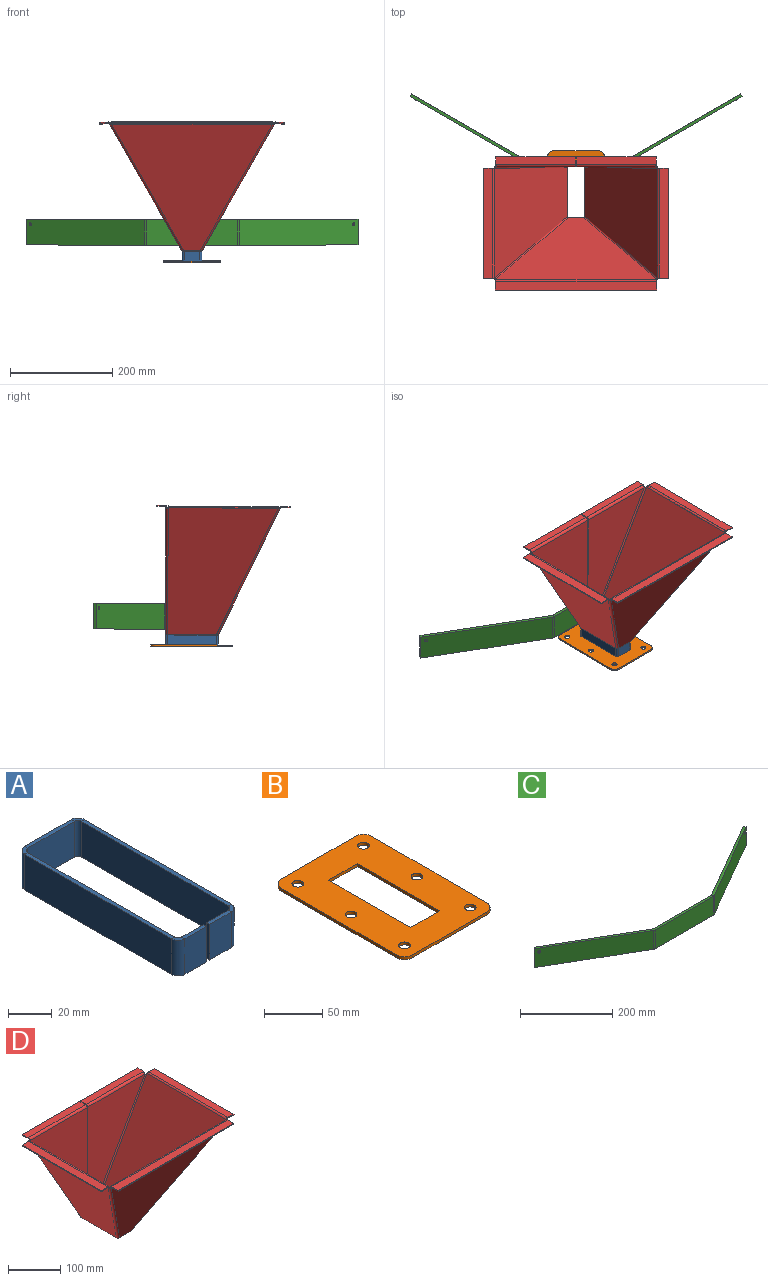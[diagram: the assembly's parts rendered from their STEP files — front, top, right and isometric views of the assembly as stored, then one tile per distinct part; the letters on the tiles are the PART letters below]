
ASSEMBLY  parts=4 mates=3
PART A: 38 faces, bbox 39x104x20 mm
  f0: plane 30x2mm, normal (0,0,1), area 60mm2, adj f2,f3,f18,f35
  f1: plane 30x2mm, normal (0,0,-1), area 60mm2, adj f2,f3,f17,f34
  f2: plane 30x20mm, normal (0,1,0), area 600mm2, adj f0,f1,f19,f36
  f3: plane 30x20mm, normal (0,-1,0), area 600mm2, adj f0,f1,f20,f37
  f4: plane 14x2mm, normal (0,0,-1), area 28mm2, adj f5,f7,f8,f13
  f5: plane 20x2mm, normal (1,0,0), area 40mm2, adj f4,f6,f7,f8
  f6: plane 14x2mm, normal (0,0,1), area 28mm2, adj f5,f7,f8,f14
  f7: plane 20x14mm, normal (0,-1,0), area 280mm2, adj f4,f5,f6,f15
  f8: plane 20x14mm, normal (0,1,0), area 280mm2, adj f4,f5,f6,f16
  f9: plane 95x2mm, normal (0,0,1), area 190mm2, adj f11,f12,f14,f18
  f10: plane 95x2mm, normal (0,0,-1), area 190mm2, adj f11,f12,f13,f17
  f11: plane 95x20mm, normal (-1,0,0), area 1900mm2, adj f9,f10,f15,f19
  f12: plane 95x20mm, normal (1,0,0), area 1900mm2, adj f9,f10,f16,f20
  f13: plane 4.5x4.5mm, normal (0,0,-1), area 11mm2, adj f4,f10,f15,f16
  f14: plane 4.5x4.5mm, normal (0,0,1), area 11mm2, adj f6,f9,f15,f16
  f15: cylinder r=4.5mm len=20mm, axis (0,0,-1), area 141.4mm2, adj f7,f11,f13,f14
  f16: cylinder r=2.5mm len=20mm, axis (0,0,-1), area 78.5mm2, adj f8,f12,f13,f14
  f17: plane 4.5x4.5mm, normal (0,0,-1), area 11mm2, adj f1,f10,f19,f20
  f18: plane 4.5x4.5mm, normal (0,0,1), area 11mm2, adj f0,f9,f19,f20
  f19: cylinder r=4.5mm len=20mm, axis (0,0,-1), area 141.4mm2, adj f2,f11,f17,f18
  f20: cylinder r=2.5mm len=20mm, axis (0,0,-1), area 78.5mm2, adj f3,f12,f17,f18
  f21: plane 14x2mm, normal (0,0,-1), area 28mm2, adj f23,f24,f25,f30
  f22: plane 14x2mm, normal (0,0,1), area 28mm2, adj f23,f24,f25,f31
  f23: plane 20x2mm, normal (-1,0,0), area 40mm2, adj f21,f22,f24,f25
  f24: plane 20x14mm, normal (0,-1,0), area 280mm2, adj f21,f22,f23,f32
  f25: plane 20x14mm, normal (0,1,0), area 280mm2, adj f21,f22,f23,f33
  f26: plane 95x2mm, normal (0,0,1), area 190mm2, adj f28,f29,f31,f35
  f27: plane 95x2mm, normal (0,0,-1), area 190mm2, adj f28,f29,f30,f34
  f28: plane 95x20mm, normal (1,0,0), area 1900mm2, adj f26,f27,f32,f36
  f29: plane 95x20mm, normal (-1,0,0), area 1900mm2, adj f26,f27,f33,f37
  f30: plane 4.5x4.5mm, normal (0,0,-1), area 11mm2, adj f21,f27,f32,f33
  f31: plane 4.5x4.5mm, normal (0,0,1), area 11mm2, adj f22,f26,f32,f33
  f32: cylinder r=4.5mm len=20mm, axis (0,0,-1), area 141.4mm2, adj f24,f28,f30,f31
  f33: cylinder r=2.5mm len=20mm, axis (0,0,-1), area 78.5mm2, adj f25,f29,f30,f31
  f34: plane 4.5x4.5mm, normal (0,0,-1), area 11mm2, adj f1,f27,f36,f37
  f35: plane 4.5x4.5mm, normal (0,0,1), area 11mm2, adj f0,f26,f36,f37
  f36: cylinder r=4.5mm len=20mm, axis (0,0,-1), area 141.4mm2, adj f2,f28,f34,f35
  f37: cylinder r=2.5mm len=20mm, axis (0,0,-1), area 78.5mm2, adj f3,f29,f34,f35
PART B: 20 faces, bbox 110x160x3 mm
  f0: plane 140x3mm, normal (1,0,0), area 420mm2, adj f1,f17,f18,f19
  f1: cylinder r=10mm len=10mm, axis (0,0,-1), area 47.1mm2, adj f0,f2,f18,f19
  f2: plane 90x3mm, normal (0,1,0), area 270mm2, adj f1,f3,f18,f19
  f3: cylinder r=10mm len=10mm, axis (0,0,-1), area 47.1mm2, adj f2,f4,f18,f19
  f4: plane 140x3mm, normal (-1,0,0), area 420mm2, adj f3,f5,f18,f19
  f5: cylinder r=10mm len=10mm, axis (0,0,-1), area 47.1mm2, adj f4,f6,f18,f19
  f6: plane 90x3mm, normal (0,-1,0), area 270mm2, adj f5,f17,f18,f19
  f7: plane 100x3mm, normal (1,0,0), area 300mm2, adj f8,f16,f18,f19
  f8: plane 35x3mm, normal (0,-1,0), area 105mm2, adj f7,f9,f18,f19
  f9: plane 100x3mm, normal (-1,0,0), area 300mm2, adj f8,f16,f18,f19
  f10: cylinder r=5mm len=10mm, axis (0,0,-1), area 94.2mm2, adj f18,f19
  f11: cylinder r=5mm len=10mm, axis (0,0,-1), area 94.2mm2, adj f18,f19
  f12: cylinder r=5mm len=10mm, axis (0,0,-1), area 94.2mm2, adj f18,f19
  f13: cylinder r=5mm len=10mm, axis (0,0,-1), area 94.2mm2, adj f18,f19
  f14: cylinder r=5mm len=10mm, axis (0,0,-1), area 94.2mm2, adj f18,f19
  f15: cylinder r=5mm len=10mm, axis (0,0,-1), area 94.2mm2, adj f18,f19
  f16: plane 35x3mm, normal (0,1,0), area 105mm2, adj f7,f9,f18,f19
  f17: cylinder r=10mm len=10mm, axis (0,0,-1), area 47.1mm2, adj f0,f6,f18,f19
  f18: plane 160x110mm, normal (0,0,1), area 13542.9mm2, adj f0,f1,f2,f3,f4,f5,f6,f7
  f19: plane 160x110mm, normal (0,0,-1), area 13542.9mm2, adj f0,f1,f2,f3,f4,f5,f6,f7
PART C: 24 faces, bbox 648.5x139.5x50 mm
  f0: plane 178.66x6mm, normal (0,0,-1), area 1072mm2, adj f2,f3,f11,f21
  f1: plane 178.66x6mm, normal (0,0,1), area 1072mm2, adj f2,f3,f10,f20
  f2: plane 178.66x50mm, normal (0,1,0), area 8933mm2, adj f0,f1,f13,f23
  f3: plane 178.66x50mm, normal (0,-1,0), area 8933mm2, adj f0,f1,f12,f22
  f4: plane 233.65x138.36mm, normal (0,0,-1), area 1598mm2, adj f5,f8,f9,f11
  f5: plane 50x5.2mm, normal (-0.87,0.5,0), area 300mm2, adj f4,f6,f8,f9
  f6: plane 233.65x138.36mm, normal (0,0,1), area 1598mm2, adj f5,f8,f9,f10
  f7: cylinder r=3mm len=8.2mm, axis (0.5,0.87,0), area 113.1mm2, adj f8,f9
  f8: plane 230.65x133.17mm, normal (0.5,0.87,0), area 13288.2mm2, adj f4,f5,f6,f7,f13
  f9: plane 230.65x133.17mm, normal (-0.5,-0.87,0), area 13288.2mm2, adj f4,f5,f6,f7,f12
  f10: plane 6.34x4.25mm, normal (0,0,1), area 17.3mm2, adj f1,f6,f12,f13
  f11: plane 6.34x4.25mm, normal (0,0,-1), area 17.3mm2, adj f0,f4,f12,f13
  f12: cylinder r=8.5mm len=50mm, axis (0,0,1), area 222.5mm2, adj f3,f9,f10,f11
  f13: cylinder r=2.5mm len=50mm, axis (0,0,1), area 65.4mm2, adj f2,f8,f10,f11
  f14: plane 233.65x138.36mm, normal (0,0,-1), area 1598mm2, adj f17,f18,f19,f21
  f15: plane 233.65x138.36mm, normal (0,0,1), area 1598mm2, adj f17,f18,f19,f20
  f16: cylinder r=3mm len=8.2mm, axis (-0.5,0.87,0), area 113.1mm2, adj f18,f19
  f17: plane 50x5.2mm, normal (0.87,0.5,0), area 300mm2, adj f14,f15,f18,f19
  f18: plane 230.65x133.17mm, normal (-0.5,0.87,0), area 13288.2mm2, adj f14,f15,f16,f17,f23
  f19: plane 230.65x133.17mm, normal (0.5,-0.87,0), area 13288.2mm2, adj f14,f15,f16,f17,f22
  f20: plane 6.34x4.25mm, normal (0,0,1), area 17.3mm2, adj f1,f15,f22,f23
  f21: plane 6.34x4.25mm, normal (0,0,-1), area 17.3mm2, adj f0,f14,f22,f23
  f22: cylinder r=8.5mm len=50mm, axis (0,0,1), area 222.5mm2, adj f3,f19,f20,f21
  f23: cylinder r=2.5mm len=50mm, axis (0,0,1), area 65.4mm2, adj f2,f18,f20,f21
PART D: 88 faces, bbox 361.2x260.6x254.2 mm
  f0: plane 13.62x2mm, normal (0,0,-1), area 27.2mm2, adj f1,f2,f3,f44
  f1: plane 247.5x2mm, normal (1,0,0), area 495mm2, adj f0,f2,f3,f85
  f2: plane 247.5x154.7mm, normal (0,1,0), area 20829.6mm2, adj f0,f1,f45,f87
  f3: plane 247.5x154.7mm, normal (0,-1,0), area 20829.6mm2, adj f0,f1,f46,f86
  f4: plane 13.62x2mm, normal (0,0,-1), area 27.2mm2, adj f5,f6,f7,f35
  f5: plane 247.5x2mm, normal (-1,0,0), area 495mm2, adj f4,f6,f7,f75
  f6: plane 247.5x154.7mm, normal (0,1,0), area 20829.6mm2, adj f4,f5,f36,f77
  f7: plane 247.5x154.7mm, normal (0,-1,0), area 20829.6mm2, adj f4,f5,f37,f76
  f8: plane 4.06x3.91mm, normal (0.46,-0.38,0.8), area 9.5mm2, adj f10,f11,f19,f65
  f9: bspline ~4x3.98mm, area 10.1mm2, adj f10,f11,f12,f20
  f10: cylinder r=4.5mm len=249.33mm, axis (0.46,-0.38,0.8), area 1886.6mm2, adj f8,f9,f13,f22
  f11: cylinder r=2.5mm len=249mm, axis (0.46,-0.38,0.8), area 1048.1mm2, adj f8,f9,f14,f23
  f12: plane 30.48x1.8mm, normal (0,0.43,-0.9), area 61mm2, adj f9,f13,f14,f16
  f13: plane 313.87x248.59mm, normal (0,-0.9,-0.43), area 47476.7mm2, adj f10,f12,f17,f67
  f14: plane 313.87x248.59mm, normal (0,0.9,0.43), area 47476.7mm2, adj f11,f12,f18,f66
  f15: plane 4.06x3.91mm, normal (-0.46,-0.38,0.8), area 9.5mm2, adj f17,f18,f40,f64
  f16: bspline ~4x3.98mm, area 10.1mm2, adj f12,f17,f18,f39
  f17: cylinder r=4.5mm len=249.33mm, axis (-0.46,-0.38,0.8), area 1886.6mm2, adj f13,f15,f16,f41
  f18: cylinder r=2.5mm len=249mm, axis (-0.46,-0.38,0.8), area 1048.1mm2, adj f14,f15,f16,f42
  f19: plane 1.86x1.2mm, normal (-0.19,-0.92,-0.33), area 0.5mm2, adj f8,f22,f23,f30
  f20: plane 95.32x1.74mm, normal (-0.5,0,-0.87), area 190.6mm2, adj f9,f22,f23,f35
  f21: plane 3.37x3.09mm, normal (0,1,0), area 5.5mm2, adj f22,f23,f31,f34
  f22: plane 248.64x214.67mm, normal (0.87,0,-0.5), area 44359.5mm2, adj f10,f19,f20,f21,f33,f36
  f23: plane 248.64x214.67mm, normal (-0.87,0,0.5), area 44359.5mm2, adj f11,f19,f20,f21,f32,f37
  f24: plane 215.19x2mm, normal (1,0,-0.06), area 430.4mm2, adj f25,f27,f28,f29
  f25: plane 17.28x3.1mm, normal (0,-1,0), area 34.4mm2, adj f24,f26,f28,f29
  f26: plane 2x0.52mm, normal (-1,0,0.06), area 1mm2, adj f25,f28,f29,f30
  f27: plane 17.28x3.1mm, normal (0,1,0), area 34.4mm2, adj f24,f28,f29,f31
  f28: plane 215.19x17.15mm, normal (-0.06,0,-1), area 3698.7mm2, adj f24,f25,f26,f27,f33
  f29: plane 215.19x17.15mm, normal (0.06,0,1), area 3698.7mm2, adj f24,f25,f26,f27,f32
  f30: plane 4.2x3.26mm, normal (0,-1,0), area 7.8mm2, adj f19,f26,f32,f33
  f31: plane 4.2x3.26mm, normal (0,1,0), area 7.8mm2, adj f21,f27,f32,f33
  f32: cylinder r=4.5mm len=214.67mm, axis (0,-1,0), area 1079mm2, adj f23,f29,f30,f31
  f33: cylinder r=2.5mm len=214.67mm, axis (0,-1,0), area 599.5mm2, adj f22,f28,f30,f31
  f34: plane 4.5x3.91mm, normal (0.5,0,0.87), area 11mm2, adj f21,f36,f37,f74
  f35: bspline ~4.63x4.5mm, area 11.6mm2, adj f4,f20,f36,f37
  f36: cylinder r=4.5mm len=249.73mm, axis (0.5,0,0.87), area 2006.3mm2, adj f6,f22,f34,f35
  f37: cylinder r=2.5mm len=248.74mm, axis (0.5,0,0.87), area 1114.6mm2, adj f7,f23,f34,f35
  f38: plane 3.37x3.09mm, normal (0,1,0), area 5.5mm2, adj f41,f42,f43,f53
  f39: plane 95.32x1.74mm, normal (0.5,0,-0.87), area 190.6mm2, adj f16,f41,f42,f44
  f40: plane 1.86x1.2mm, normal (0.19,-0.92,-0.33), area 0.5mm2, adj f15,f41,f42,f54
  f41: plane 248.64x214.67mm, normal (-0.87,0,-0.5), area 44359.5mm2, adj f17,f38,f39,f40,f45,f56
  f42: plane 248.64x214.67mm, normal (0.87,0,0.5), area 44359.5mm2, adj f18,f38,f39,f40,f46,f55
  f43: plane 4.5x3.91mm, normal (-0.5,0,0.87), area 11mm2, adj f38,f45,f46,f84
  f44: bspline ~4.65x4.5mm, area 11.6mm2, adj f0,f39,f45,f46
  f45: cylinder r=4.5mm len=249.73mm, axis (-0.5,0,0.87), area 2006.3mm2, adj f2,f41,f43,f44
  f46: cylinder r=2.5mm len=248.74mm, axis (-0.5,0,0.87), area 1114.6mm2, adj f3,f42,f43,f44
  f47: plane 2x0.52mm, normal (1,0,0.06), area 1mm2, adj f50,f51,f52,f54
  f48: plane 215.19x2mm, normal (-1,0,-0.06), area 430.4mm2, adj f49,f50,f51,f52
  f49: plane 17.28x3.1mm, normal (0,1,0), area 34.4mm2, adj f48,f51,f52,f53
  f50: plane 17.28x3.1mm, normal (0,-1,0), area 34.4mm2, adj f47,f48,f51,f52
  f51: plane 215.19x17.15mm, normal (0.06,0,-1), area 3698.7mm2, adj f47,f48,f49,f50,f56
  f52: plane 215.19x17.15mm, normal (-0.06,0,1), area 3698.7mm2, adj f47,f48,f49,f50,f55
  f53: plane 4.2x3.26mm, normal (0,1,0), area 7.8mm2, adj f38,f49,f55,f56
  f54: plane 4.2x3.26mm, normal (0,-1,0), area 7.8mm2, adj f40,f47,f55,f56
  f55: cylinder r=4.5mm len=214.67mm, axis (0,1,0), area 1079mm2, adj f42,f52,f53,f54
  f56: cylinder r=2.5mm len=214.67mm, axis (0,1,0), area 599.5mm2, adj f41,f51,f53,f54
  f57: plane 2x0.64mm, normal (0,1,-0.01), area 1.3mm2, adj f61,f62,f63,f65
  f58: plane 315.16x2mm, normal (0,-1,0.01), area 630.3mm2, adj f59,f61,f62,f63
  f59: plane 17.2x2.11mm, normal (-1,0,0), area 34.4mm2, adj f58,f60,f62,f63
  f60: plane 2x0.64mm, normal (0,1,-0.01), area 1.3mm2, adj f59,f62,f63,f64
  f61: plane 17.2x2.11mm, normal (1,0,0), area 34.4mm2, adj f57,f58,f62,f63
  f62: plane 315.16x17.19mm, normal (0,-0.01,-1), area 5416.9mm2, adj f57,f58,f59,f60,f61,f67
  f63: plane 315.16x17.19mm, normal (0,0.01,1), area 5416.9mm2, adj f57,f58,f59,f60,f61,f66
  f64: plane 4.04x3.42mm, normal (-1,0,0), area 7.8mm2, adj f15,f60,f66,f67
  f65: plane 4.04x3.42mm, normal (1,0,0), area 7.8mm2, adj f8,f57,f66,f67
  f66: cylinder r=4.5mm len=313.87mm, axis (-1,0,0), area 1577.7mm2, adj f14,f63,f64,f65
  f67: cylinder r=2.5mm len=313.87mm, axis (-1,0,0), area 876.5mm2, adj f13,f62,f64,f65
  f68: plane 155.84x2mm, normal (0,1,0), area 311.7mm2, adj f69,f71,f72,f73
  f69: plane 15.5x2mm, normal (1,0,0), area 31mm2, adj f68,f70,f72,f73
  f70: plane 2x1.14mm, normal (0,-1,0), area 2.3mm2, adj f69,f72,f73,f74
  f71: plane 15.5x2mm, normal (-1,0,0), area 31mm2, adj f68,f72,f73,f75
  f72: plane 155.84x15.5mm, normal (0,0,-1), area 2415.5mm2, adj f68,f69,f70,f71,f77
  f73: plane 155.84x15.5mm, normal (0,0,1), area 2415.5mm2, adj f68,f69,f70,f71,f76
  f74: plane 4.5x4.5mm, normal (1,0,0), area 11mm2, adj f34,f70,f76,f77
  f75: plane 4.5x4.5mm, normal (-1,0,0), area 11mm2, adj f5,f71,f76,f77
  f76: cylinder r=4.5mm len=154.7mm, axis (1,0,0), area 1093.5mm2, adj f7,f73,f74,f75
  f77: cylinder r=2.5mm len=154.7mm, axis (1,0,0), area 607.5mm2, adj f6,f72,f74,f75
  f78: plane 2x1.14mm, normal (0,-1,0), area 2.3mm2, adj f81,f82,f83,f84
  f79: plane 155.84x2mm, normal (0,1,0), area 311.7mm2, adj f80,f81,f82,f83
  f80: plane 15.5x2mm, normal (1,0,0), area 31mm2, adj f79,f82,f83,f85
  f81: plane 15.5x2mm, normal (-1,0,0), area 31mm2, adj f78,f79,f82,f83
  f82: plane 155.84x15.5mm, normal (0,0,-1), area 2415.5mm2, adj f78,f79,f80,f81,f87
  f83: plane 155.84x15.5mm, normal (0,0,1), area 2415.5mm2, adj f78,f79,f80,f81,f86
  f84: plane 4.5x4.5mm, normal (-1,0,0), area 11mm2, adj f43,f78,f86,f87
  f85: plane 4.5x4.5mm, normal (1,0,0), area 11mm2, adj f1,f80,f86,f87
  f86: cylinder r=4.5mm len=154.7mm, axis (-1,0,0), area 1093.5mm2, adj f3,f83,f84,f85
  f87: cylinder r=2.5mm len=154.7mm, axis (-1,0,0), area 607.5mm2, adj f2,f82,f84,f85
PLACE A rot(axis=(-1,0,0),179.6deg) t=(345.65,192.11,-250.05)mm
PLACE B rot(axis=(1,0,0),0.4deg) t=(-380,192.26,-273.05)mm
PLACE C rot(axis=(1,0,0),0.4deg) t=(0,82.35,-240.74)mm
PLACE D rot(axis=(1,0,0),0.4deg) t=(0,192.11,-250.05)mm
MATE fastened D.f0 <-> A.f10  axis (0,-0.01,1) through (0,192.11,-250.05)mm
MATE fastened B.f18 <-> A.f9  axis (0,-0.01,1) through (0,192.24,-270.05)mm
MATE fastened C.f3 <-> D.f6  axis (0,-1,-0.01) through (0,243.89,-214.73)mm
